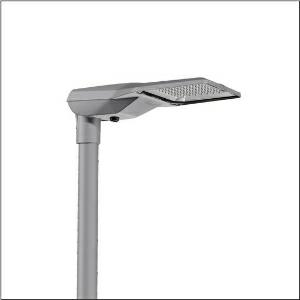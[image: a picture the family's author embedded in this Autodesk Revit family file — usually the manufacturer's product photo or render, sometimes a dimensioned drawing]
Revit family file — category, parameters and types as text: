
# Revit family: streetlight_sl_21_iq_midi___p0_8a_5xe3u31u08nb_8349
name_source: partatom
category: Lighting Fixtures
units: mm (PartAtom-declared; Revit-internal decimal feet)

## family parameters
Cut with Voids When Loaded = No
Host = Face
Light Source = No
Part Type = Normal
Room Calculation Point = No
Round Connector Dimension = Use Diameter
Shared = No

## types (1)
- --- (1 x LED, 21740 lm, 136.6 W, 3000K)
    Apparent Load = 137 VA
    CIE Flux Codes = 36 69 97 100 100
    Color Rendering = 70
    Color Temperature = 3000K
    Default Elevation = 1800 mm
    Description = Streetlight SL 21 iQ midi, mast luminaire, primary light control with lens, of PMMA, primary optical cover: cover, of toughened safety glass, transparent, light distribution: P0.8a, light emission: direct distribution, primary light characteristic: asymmetric, installation type: post-top, side-entry, LED, High Power LED, rated luminous flux: 21.740lm, luminous efficacy: 159lm/W, light colour: 730, colour temperature: 3000K, control gear: iQ-Street Remote, D4i with power reduction, control: pre-setting: logarithmic dimming characteristic, Street-Remote, Auto-Match, Temp-Guard, Lumen-Switch, Night-Set, Smart-Wire, Light-Fading, Desk-Remote (wireless, voltage-free reading and setting of iQ features in the workshop via application-optimized NFC function/RFID function), optimised constant luminous flux control (CLO 2.0), mains connection: 230..240V, AC, 50/60Hz, start of lifetime: 137W, end of service life: 144W, reduction: 61W, luminaire housing, of diecast aluminium, powder-coated, SITECO metallic grey (DB 702S), corrosivity category C5 high according to DIN EN ISO 12944, please order mast flange separately, inclination adjustable: 0°, 5°, 10°, 15°, sealing non-destructively replaceable, multi-level sealing system, length: 644mm, width: 335mm, height: 110mm, mast flange for spigot size: 42mm (side-entry): 5XC10008XM4, 60/48mm (side-entry/post-top): 5XC10108XM2, 76/60mm (side-entry/post-top): 5XC10108XM1, mounting height: 4..8m, Smart Interface below, protection rating (complete): IP66, insulation class (complete): insulation class II (safety insulation), certification: CE, ENEC, ENEC+, VDE, impact resistance: IK10, permissible operating ambient temperature for outdoor applications: -40..+50°C, standard-compliant lighting for roads and squares, packaging unit: 1 piece

Light Distribution: P0.8a
    Height = 111 mm
    Lamp = 1 x LED
    Lamp Light Flux = 21740 lm
    Lamp Power = 136.6 W
    Lamp count = 1
    Length = 644 mm
    Luminous efficacy = 159 lm/W
    Manufacturer = Siteco
    ModVariant = No
    Model = 5XE3U31U08NB
    Number of Poles = 1
    OnlyDefault = Yes
    Power Factor = 1
    Product Name = Streetlight SL 21 iQ midi | P0.8a
    Product group = mast luminaire | pylon top
    ProductGroupID = 6100
    Protection Class = Protection class II
    Protection Degree = IP 66
    RLX_Detail_Level = 1
    RLX_Emergency_Light_Flux = 0 lm
    RLX_Emergency_Type = 0
    RLX_Emergency_Type_DB = No
    RlxData = <blob elided: 92705 chars, md5=ea6c38c8>
    Socket = socket
    Standby Power = 0 W
    System Light Flux = 21740 lm
    System Power = 137 W
    Type Comments = factory setting: luminous flux: 100 % | dim-lin: 254 | 733 mA
    Type Image = l_1004300.jpg
    URL = http://relux.com
    VarID = @adj_079801
    Voltage = 0 V
    Weight = 0.00 kg
    Width = 336 mm

## geometry (parser evidence)
native form markers: Blend x4, Sweep x11
no freeform markers — native parametric forms only
